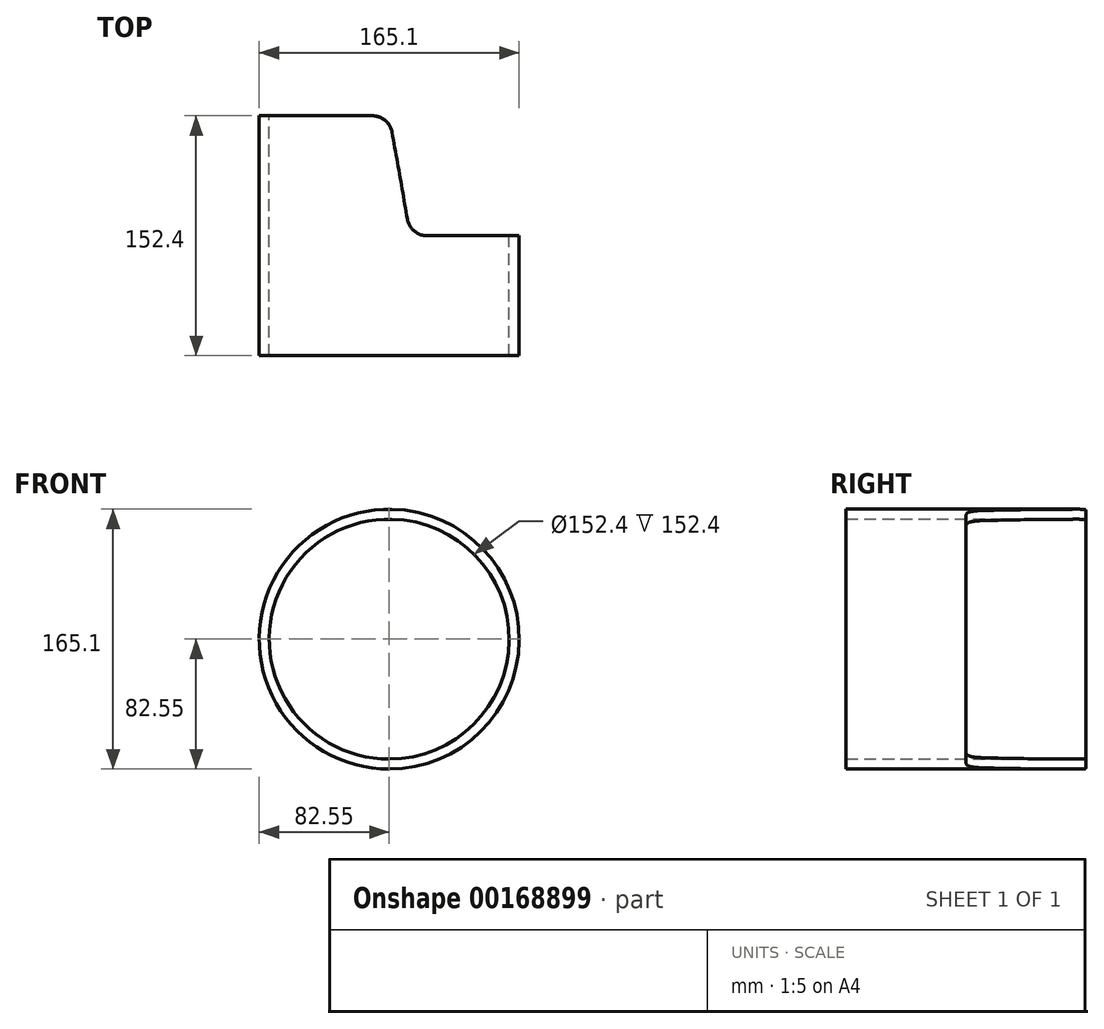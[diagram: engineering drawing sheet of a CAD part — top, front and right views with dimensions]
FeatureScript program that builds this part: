
annotation { "Feature Type Name" : "Feature", "Feature Type Description" : "" }
export const myFeature = defineFeature(function(context is Context, id is Id, definition is map)
    precondition{}
    {
        {
            var Q0;
            Q0=qCreatedBy(makeId("Front.planeOp"),FACE);
            var sketch = newSketch(context, id + "F0", { "sketchPlane" : qUnion([Q0])});
            skCircle(sketch, "E0", {"center": v(0, 0) * mm, "radius": 76.2 * mm});
            skCircle(sketch, "E1.0", {"center": v(0, 0) * mm, "radius": 82.55 * mm});
            skSolve(sketch);
        }
        {
            var Q0;
            Q0 = qSketchRegion(id + "F0", true);
            extrude(context, id + "F1", {"entities" : qUnion([Q0]), "depth" : 152.4 * mm});
        }
        {
            var Q0;
            Q0=qCreatedBy(makeId("Top.planeOp"),FACE);
            var sketch = newSketch(context, id + "F2", { "sketchPlane" : qUnion([Q0])});
            skLineSegment(sketch, "E2", {"start": v(1.85, -10.5) * mm, "end": v(11.59, -65.7) * mm});
            skLineSegment(sketch, "E3", {"start": v(24.1, -76.2) * mm, "end": v(82.55, -76.2) * mm});
            skLineSegment(sketch, "E4", {"start": v(82.55, 0) * mm, "end": v(82.55, -76.2) * mm});
            skPoint(sketch, "E5.visualSharp", {"position": v(13.44, -76.2) * mm});
            skArc(sketch, "E5.filletArc", {"start": v(11.59, -65.7) * mm, "mid": v(15.93, -73.23) * mm, "end": v(24.1, -76.2) * mm});
            skPoint(sketch, "E6.newPointB", {"position": v(82.55, 0) * mm});
            skArc(sketch, "E6.filletArc", {"start": v(1.85, -10.5) * mm, "mid": v(-2.5, -2.97) * mm, "end": v(-10.66, 0) * mm});
            skPoint(sketch, "E7", {"position": v(0, 0) * mm});
            skLineSegment(sketch, "E8", {"start": v(-10.66, 0) * mm, "end": v(82.55, 0) * mm});
            skPoint(sketch, "E9.0.end.orphan", {"position": v(-82.55, 0) * mm});
            skSolve(sketch);
        }
        {
            var Q0;
            Q0 = qSketchRegion(id + "F2", true);
            extrude(context, id + "F3", {"entities" : qUnion([Q0]), "operationType" : NewBodyOperationType.REMOVE, "endBound" : BoundingType.THROUGH_ALL, "oppositeDirection" : true, "depth" : 25.4 * mm, "hasSecondDirection" : true, "secondDirectionBound" : SecondDirectionBoundingType.THROUGH_ALL, "secondDirectionOppositeDirection" : false, "secondDirectionDepth" : 25.4 * mm});
        }
    });
